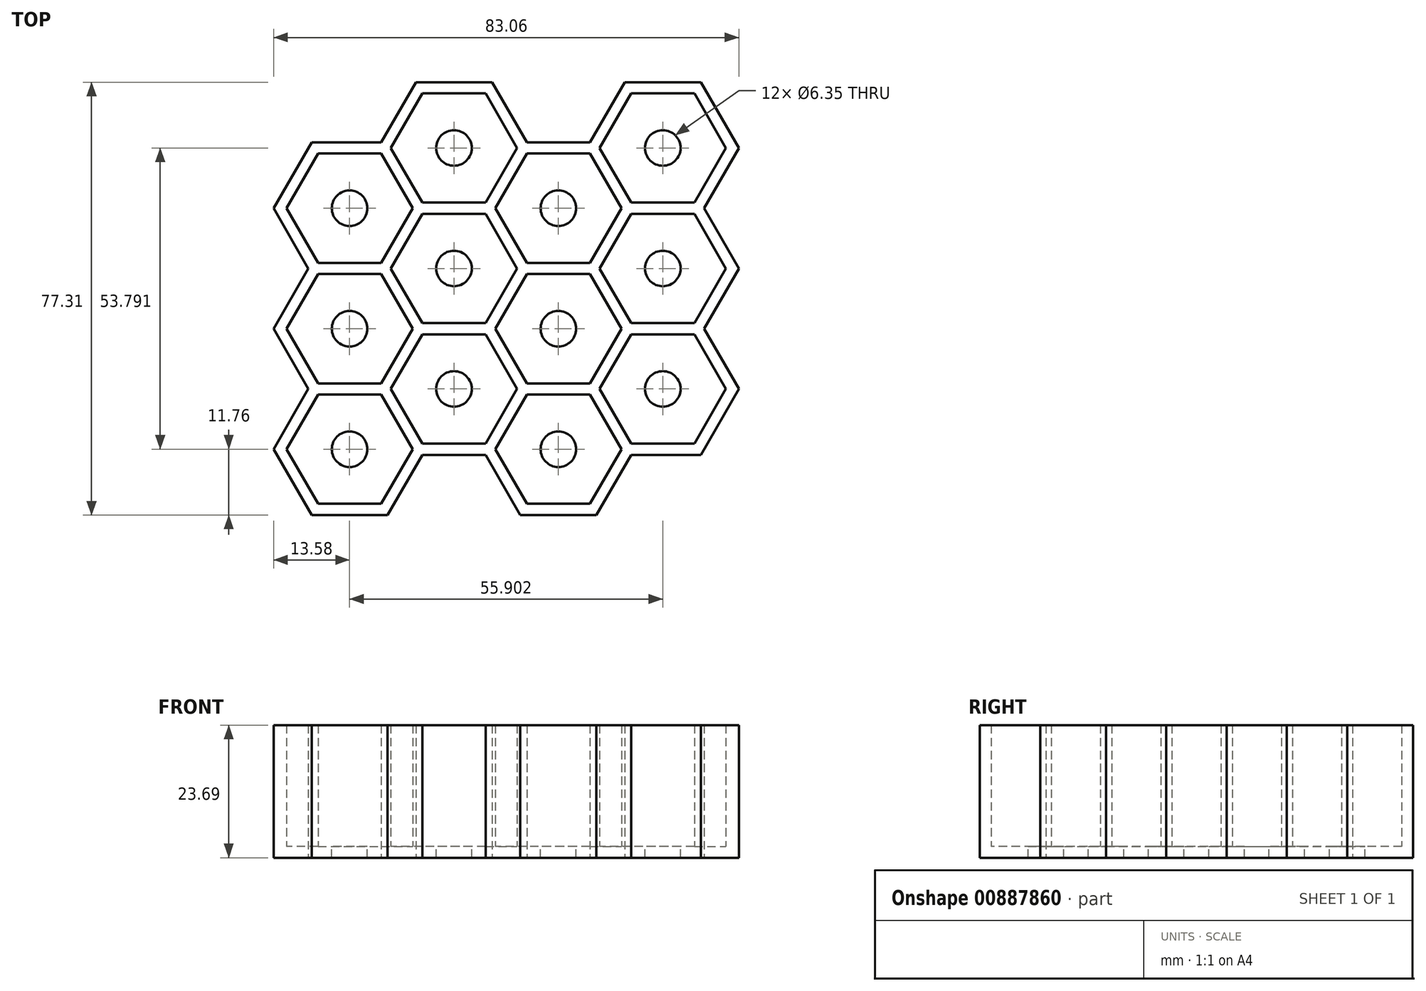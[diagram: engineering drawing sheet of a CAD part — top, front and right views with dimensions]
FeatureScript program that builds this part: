
annotation { "Feature Type Name" : "Feature", "Feature Type Description" : "" }
export const myFeature = defineFeature(function(context is Context, id is Id, definition is map)
    precondition{}
    {
        {
            var Q0;
            Q0=qCreatedBy(makeId("Top.planeOp"),FACE);
            var sketch = newSketch(context, id + "F0", { "sketchPlane" : qUnion([Q0])});
            skCircle(sketch, "E0.cCircle", {"center": v(0, 0) * mm, "radius": 9.76 * mm, "construction": true});
            skLineSegment(sketch, "E0.0", {"start": v(5.63, 9.76) * mm, "end": v(11.27, 0) * mm});
            skLineSegment(sketch, "E0.1", {"start": v(11.27, 0) * mm, "end": v(5.63, -9.76) * mm});
            skLineSegment(sketch, "E0.2", {"start": v(5.63, -9.76) * mm, "end": v(-5.63, -9.76) * mm});
            skLineSegment(sketch, "E0.3", {"start": v(-5.63, -9.76) * mm, "end": v(-11.27, 0) * mm});
            skLineSegment(sketch, "E0.4", {"start": v(-11.27, 0) * mm, "end": v(-5.63, 9.76) * mm});
            skLineSegment(sketch, "E0.5", {"start": v(-5.63, 9.76) * mm, "end": v(5.63, 9.76) * mm});
            skPoint(sketch, "E0.0.midPoint", {"position": v(8.45, 4.88) * mm});
            skPoint(sketch, "E1.0.1.0", {"position": v(8.45, 26.4) * mm});
            skLineSegment(sketch, "E1.0.1.1", {"start": v(5.63, 11.76) * mm, "end": v(-5.63, 11.76) * mm});
            skLineSegment(sketch, "E1.0.1.2", {"start": v(-5.63, 31.27) * mm, "end": v(5.63, 31.27) * mm});
            skCircle(sketch, "E1.0.1.3", {"center": v(0, 21.52) * mm, "radius": 9.76 * mm, "construction": true});
            skLineSegment(sketch, "E1.0.1.4", {"start": v(-5.63, 11.76) * mm, "end": v(-11.27, 21.52) * mm});
            skLineSegment(sketch, "E1.0.1.5", {"start": v(-11.27, 21.52) * mm, "end": v(-5.63, 31.27) * mm});
            skLineSegment(sketch, "E1.0.1.6", {"start": v(5.63, 31.27) * mm, "end": v(11.27, 21.52) * mm});
            skLineSegment(sketch, "E1.0.1.7", {"start": v(11.27, 21.52) * mm, "end": v(5.63, 11.76) * mm});
            skPoint(sketch, "E1.0.2.0", {"position": v(8.45, 47.91) * mm});
            skLineSegment(sketch, "E1.0.2.1", {"start": v(5.63, 33.27) * mm, "end": v(-5.63, 33.27) * mm});
            skLineSegment(sketch, "E1.0.2.2", {"start": v(-5.63, 52.8) * mm, "end": v(5.63, 52.8) * mm});
            skCircle(sketch, "E1.0.2.3", {"center": v(0, 43.03) * mm, "radius": 9.76 * mm, "construction": true});
            skLineSegment(sketch, "E1.0.2.4", {"start": v(-5.63, 33.27) * mm, "end": v(-11.27, 43.03) * mm});
            skLineSegment(sketch, "E1.0.2.5", {"start": v(-11.27, 43.03) * mm, "end": v(-5.63, 52.8) * mm});
            skLineSegment(sketch, "E1.0.2.6", {"start": v(5.63, 52.8) * mm, "end": v(11.27, 43.03) * mm});
            skLineSegment(sketch, "E1.0.2.7", {"start": v(11.27, 43.03) * mm, "end": v(5.63, 33.27) * mm});
            skLineSegment(sketch, "E1.direction1", {"start": v(-5.63, -9.76) * mm, "end": v(27.15, -9.76) * mm, "construction": true});
            skLineSegment(sketch, "E1.direction2", {"start": v(-5.63, -9.76) * mm, "end": v(-5.63, 11.76) * mm, "construction": true});
            skCircle(sketch, "E2.cCircle", {"center": v(18.63, 10.76) * mm, "radius": 9.76 * mm, "construction": true});
            skLineSegment(sketch, "E2.0", {"start": v(24.27, 20.52) * mm, "end": v(29.9, 10.76) * mm});
            skLineSegment(sketch, "E2.1", {"start": v(29.9, 10.76) * mm, "end": v(24.27, 1) * mm});
            skLineSegment(sketch, "E2.2", {"start": v(24.27, 1) * mm, "end": v(13, 1) * mm});
            skLineSegment(sketch, "E2.3", {"start": v(13, 1) * mm, "end": v(7.37, 10.76) * mm});
            skLineSegment(sketch, "E2.4", {"start": v(7.37, 10.76) * mm, "end": v(13, 20.52) * mm});
            skLineSegment(sketch, "E2.5", {"start": v(13, 20.52) * mm, "end": v(24.27, 20.52) * mm});
            skPoint(sketch, "E2.0.midPoint", {"position": v(27.08, 15.64) * mm});
            skLineSegment(sketch, "E3.direction1", {"start": v(13, 1) * mm, "end": v(89.43, 1) * mm, "construction": true});
            skLineSegment(sketch, "E3.direction2", {"start": v(13, 1) * mm, "end": v(13, 51.8) * mm, "construction": true});
            skCircle(sketch, "E4.0.1.0", {"center": v(18.63, 32.27) * mm, "radius": 9.76 * mm, "construction": true});
            skPoint(sketch, "E4.0.1.1", {"position": v(27.08, 37.15) * mm});
            skLineSegment(sketch, "E4.0.1.2", {"start": v(13, 22.52) * mm, "end": v(89.43, 22.52) * mm, "construction": true});
            skLineSegment(sketch, "E4.0.1.3", {"start": v(13, 22.52) * mm, "end": v(7.37, 32.27) * mm});
            skLineSegment(sketch, "E4.0.1.4", {"start": v(13, 22.52) * mm, "end": v(13, 73.32) * mm, "construction": true});
            skLineSegment(sketch, "E4.0.1.5", {"start": v(29.9, 32.27) * mm, "end": v(24.27, 22.52) * mm});
            skLineSegment(sketch, "E4.0.1.6", {"start": v(13, 42.03) * mm, "end": v(24.27, 42.03) * mm});
            skLineSegment(sketch, "E4.0.1.7", {"start": v(7.37, 32.27) * mm, "end": v(13, 42.03) * mm});
            skLineSegment(sketch, "E4.0.1.8", {"start": v(24.27, 22.52) * mm, "end": v(13, 22.52) * mm});
            skLineSegment(sketch, "E4.0.1.9", {"start": v(24.27, 42.03) * mm, "end": v(29.9, 32.27) * mm});
            skCircle(sketch, "E4.0.2.0", {"center": v(18.63, 53.8) * mm, "radius": 9.76 * mm, "construction": true});
            skPoint(sketch, "E4.0.2.1", {"position": v(27.08, 58.67) * mm});
            skLineSegment(sketch, "E4.0.2.2", {"start": v(13, 44.03) * mm, "end": v(89.43, 44.03) * mm, "construction": true});
            skLineSegment(sketch, "E4.0.2.3", {"start": v(13, 44.03) * mm, "end": v(7.37, 53.8) * mm});
            skLineSegment(sketch, "E4.0.2.4", {"start": v(13, 44.03) * mm, "end": v(13, 94.83) * mm, "construction": true});
            skLineSegment(sketch, "E4.0.2.5", {"start": v(29.9, 53.8) * mm, "end": v(24.27, 44.03) * mm});
            skLineSegment(sketch, "E4.0.2.6", {"start": v(13, 63.55) * mm, "end": v(24.27, 63.55) * mm});
            skLineSegment(sketch, "E4.0.2.7", {"start": v(7.37, 53.8) * mm, "end": v(13, 63.55) * mm});
            skLineSegment(sketch, "E4.0.2.8", {"start": v(24.27, 44.03) * mm, "end": v(13, 44.03) * mm});
            skLineSegment(sketch, "E4.0.2.9", {"start": v(24.27, 63.55) * mm, "end": v(29.9, 53.8) * mm});
            skLineSegment(sketch, "E4.direction1", {"start": v(13, 1) * mm, "end": v(50.9, 1) * mm, "construction": true});
            skLineSegment(sketch, "E4.direction2", {"start": v(13, 1) * mm, "end": v(13, 22.52) * mm, "construction": true});
            skLineSegment(sketch, "E5.1.0.0", {"start": v(31.63, -9.76) * mm, "end": v(31.63, 11.76) * mm, "construction": true});
            skLineSegment(sketch, "E5.1.0.1", {"start": v(31.63, 31.27) * mm, "end": v(42.9, 31.27) * mm});
            skLineSegment(sketch, "E5.1.0.3", {"start": v(31.63, 52.8) * mm, "end": v(42.9, 52.8) * mm});
            skPoint(sketch, "E5.1.0.4", {"position": v(45.72, 47.91) * mm});
            skPoint(sketch, "E5.1.0.5", {"position": v(45.72, 26.4) * mm});
            skCircle(sketch, "E5.1.0.6", {"center": v(37.27, 21.52) * mm, "radius": 9.76 * mm, "construction": true});
            skCircle(sketch, "E5.1.0.7", {"center": v(37.27, 0) * mm, "radius": 9.76 * mm, "construction": true});
            skLineSegment(sketch, "E5.1.0.9", {"start": v(42.9, 11.76) * mm, "end": v(31.63, 11.76) * mm});
            skCircle(sketch, "E5.1.0.10", {"center": v(37.27, 43.03) * mm, "radius": 9.76 * mm, "construction": true});
            skPoint(sketch, "E5.1.0.11", {"position": v(45.72, 4.88) * mm});
            skLineSegment(sketch, "E5.1.0.12", {"start": v(42.9, -9.76) * mm, "end": v(31.63, -9.76) * mm});
            skLineSegment(sketch, "E5.1.0.13", {"start": v(42.9, 33.27) * mm, "end": v(31.63, 33.27) * mm});
            skLineSegment(sketch, "E5.1.0.16", {"start": v(48.54, 0) * mm, "end": v(42.9, -9.76) * mm});
            skLineSegment(sketch, "E5.1.0.17", {"start": v(42.9, 9.76) * mm, "end": v(48.54, 0) * mm});
            skLineSegment(sketch, "E5.1.0.20", {"start": v(31.63, 11.76) * mm, "end": v(26, 21.52) * mm});
            skLineSegment(sketch, "E5.1.0.21", {"start": v(42.9, 31.27) * mm, "end": v(48.54, 21.52) * mm});
            skLineSegment(sketch, "E5.1.0.22", {"start": v(48.54, 21.52) * mm, "end": v(42.9, 11.76) * mm});
            skLineSegment(sketch, "E5.1.0.23", {"start": v(26, 0) * mm, "end": v(31.63, 9.76) * mm});
            skLineSegment(sketch, "E5.1.0.24", {"start": v(31.63, 9.76) * mm, "end": v(42.9, 9.76) * mm});
            skLineSegment(sketch, "E5.1.0.25", {"start": v(31.63, -9.76) * mm, "end": v(26, 0) * mm});
            skLineSegment(sketch, "E5.1.0.27", {"start": v(48.54, 43.03) * mm, "end": v(42.9, 33.27) * mm});
            skLineSegment(sketch, "E5.1.0.28", {"start": v(26, 21.52) * mm, "end": v(31.63, 31.27) * mm});
            skLineSegment(sketch, "E5.1.0.29", {"start": v(26, 43.03) * mm, "end": v(31.63, 52.8) * mm});
            skLineSegment(sketch, "E5.1.0.30", {"start": v(42.9, 52.8) * mm, "end": v(48.54, 43.03) * mm});
            skLineSegment(sketch, "E5.1.0.32", {"start": v(31.63, 33.27) * mm, "end": v(26, 43.03) * mm});
            skLineSegment(sketch, "E5.direction1", {"start": v(-5.63, -9.76) * mm, "end": v(31.63, -9.76) * mm, "construction": true});
            skLineSegment(sketch, "E6.0", {"start": v(-13.58, 21.52) * mm, "end": v(-7.37, 32.27) * mm});
            skLineSegment(sketch, "E6.1", {"start": v(-7.37, 10.76) * mm, "end": v(-13.58, 21.52) * mm});
            skLineSegment(sketch, "E7.0", {"start": v(-13.58, 0) * mm, "end": v(-7.37, 10.76) * mm});
            skLineSegment(sketch, "E7.1", {"start": v(-6.79, -11.76) * mm, "end": v(-13.58, 0) * mm});
            skLineSegment(sketch, "E7.2", {"start": v(6.79, -11.76) * mm, "end": v(-6.79, -11.76) * mm});
            skLineSegment(sketch, "E7.3", {"start": v(13, -1) * mm, "end": v(6.79, -11.76) * mm});
            skCircle(sketch, "E8.1.0.1", {"center": v(55.9, 32.27) * mm, "radius": 9.76 * mm, "construction": true});
            skPoint(sketch, "E8.1.0.2", {"position": v(64.35, 58.67) * mm});
            skLineSegment(sketch, "E8.1.0.3", {"start": v(50.27, 44.03) * mm, "end": v(50.27, 94.83) * mm, "construction": true});
            skLineSegment(sketch, "E8.1.0.4", {"start": v(50.27, 1) * mm, "end": v(50.27, 51.8) * mm, "construction": true});
            skLineSegment(sketch, "E8.1.0.5", {"start": v(50.27, 22.52) * mm, "end": v(50.27, 73.32) * mm, "construction": true});
            skPoint(sketch, "E8.1.0.6", {"position": v(64.35, 15.64) * mm});
            skCircle(sketch, "E8.1.0.9", {"center": v(55.9, 10.76) * mm, "radius": 9.76 * mm, "construction": true});
            skPoint(sketch, "E8.1.0.10", {"position": v(64.35, 37.15) * mm});
            skCircle(sketch, "E8.1.0.11", {"center": v(55.9, 53.8) * mm, "radius": 9.76 * mm, "construction": true});
            skLineSegment(sketch, "E8.1.0.14", {"start": v(61.54, 22.52) * mm, "end": v(50.27, 22.52) * mm});
            skLineSegment(sketch, "E8.1.0.15", {"start": v(61.54, 42.03) * mm, "end": v(67.17, 32.27) * mm});
            skLineSegment(sketch, "E8.1.0.16", {"start": v(61.54, 63.55) * mm, "end": v(67.17, 53.8) * mm});
            skLineSegment(sketch, "E8.1.0.17", {"start": v(50.27, 1) * mm, "end": v(44.63, 10.76) * mm});
            skLineSegment(sketch, "E8.1.0.18", {"start": v(61.54, 1) * mm, "end": v(50.27, 1) * mm});
            skLineSegment(sketch, "E8.1.0.21", {"start": v(50.27, 22.52) * mm, "end": v(44.63, 32.27) * mm});
            skLineSegment(sketch, "E8.1.0.22", {"start": v(50.27, 42.03) * mm, "end": v(61.54, 42.03) * mm});
            skLineSegment(sketch, "E8.1.0.23", {"start": v(50.27, 1) * mm, "end": v(50.27, 22.52) * mm, "construction": true});
            skLineSegment(sketch, "E8.1.0.24", {"start": v(61.54, 44.03) * mm, "end": v(50.27, 44.03) * mm});
            skLineSegment(sketch, "E8.1.0.26", {"start": v(44.63, 32.27) * mm, "end": v(50.27, 42.03) * mm});
            skLineSegment(sketch, "E8.1.0.29", {"start": v(67.17, 53.8) * mm, "end": v(61.54, 44.03) * mm});
            skLineSegment(sketch, "E8.1.0.30", {"start": v(50.27, 44.03) * mm, "end": v(44.63, 53.8) * mm});
            skLineSegment(sketch, "E8.1.0.31", {"start": v(44.63, 53.8) * mm, "end": v(50.27, 63.55) * mm});
            skLineSegment(sketch, "E8.1.0.32", {"start": v(50.27, 20.52) * mm, "end": v(61.54, 20.52) * mm});
            skLineSegment(sketch, "E8.1.0.33", {"start": v(44.63, 10.76) * mm, "end": v(50.27, 20.52) * mm});
            skLineSegment(sketch, "E8.1.0.34", {"start": v(67.17, 32.27) * mm, "end": v(61.54, 22.52) * mm});
            skLineSegment(sketch, "E8.1.0.36", {"start": v(50.27, 63.55) * mm, "end": v(61.54, 63.55) * mm});
            skLineSegment(sketch, "E8.1.0.37", {"start": v(67.17, 10.76) * mm, "end": v(61.54, 1) * mm});
            skLineSegment(sketch, "E8.1.0.38", {"start": v(61.54, 20.52) * mm, "end": v(67.17, 10.76) * mm});
            skLineSegment(sketch, "E8.direction1", {"start": v(25.5, -2.85) * mm, "end": v(64.28, -2.85) * mm, "construction": true});
            skLineSegment(sketch, "E9.0", {"start": v(69.48, 32.27) * mm, "end": v(63.27, 21.52) * mm});
            skLineSegment(sketch, "E9.1", {"start": v(63.27, 43.03) * mm, "end": v(69.48, 32.27) * mm});
            skLineSegment(sketch, "E10.0", {"start": v(62.7, -1) * mm, "end": v(50.27, -1) * mm});
            skLineSegment(sketch, "E10.1", {"start": v(69.48, 10.76) * mm, "end": v(62.7, -1) * mm});
            skLineSegment(sketch, "E10.2", {"start": v(63.27, 21.52) * mm, "end": v(69.48, 10.76) * mm});
            skLineSegment(sketch, "E11.0", {"start": v(30.48, -11.76) * mm, "end": v(24.27, -1) * mm});
            skLineSegment(sketch, "E11.1", {"start": v(44.06, -11.76) * mm, "end": v(30.48, -11.76) * mm});
            skLineSegment(sketch, "E11.2", {"start": v(50.27, -1) * mm, "end": v(44.06, -11.76) * mm});
            skLineSegment(sketch, "E12.0", {"start": v(24.27, -1) * mm, "end": v(13, -1) * mm});
            skLineSegment(sketch, "E13.0", {"start": v(-6.79, 54.8) * mm, "end": v(5.63, 54.8) * mm});
            skLineSegment(sketch, "E13.1", {"start": v(-13.58, 43.03) * mm, "end": v(-6.79, 54.8) * mm});
            skLineSegment(sketch, "E13.2", {"start": v(-7.37, 32.27) * mm, "end": v(-13.58, 43.03) * mm});
            skLineSegment(sketch, "E14.0", {"start": v(25.42, 65.55) * mm, "end": v(31.63, 54.8) * mm});
            skLineSegment(sketch, "E14.1", {"start": v(11.85, 65.55) * mm, "end": v(25.42, 65.55) * mm});
            skLineSegment(sketch, "E14.2", {"start": v(5.63, 54.8) * mm, "end": v(11.85, 65.55) * mm});
            skLineSegment(sketch, "E15.0", {"start": v(31.63, 54.8) * mm, "end": v(42.9, 54.8) * mm});
            skLineSegment(sketch, "E16.0", {"start": v(69.48, 53.8) * mm, "end": v(63.27, 43.03) * mm});
            skLineSegment(sketch, "E16.1", {"start": v(62.7, 65.55) * mm, "end": v(69.48, 53.8) * mm});
            skLineSegment(sketch, "E16.2", {"start": v(49.11, 65.55) * mm, "end": v(62.7, 65.55) * mm});
            skLineSegment(sketch, "E16.3", {"start": v(42.9, 54.8) * mm, "end": v(49.11, 65.55) * mm});
            skCircle(sketch, "E17", {"center": v(0, 0) * mm, "radius": 3.18 * mm});
            skCircle(sketch, "E18", {"center": v(0, 21.52) * mm, "radius": 3.18 * mm});
            skCircle(sketch, "E19", {"center": v(0, 43.03) * mm, "radius": 3.18 * mm});
            skCircle(sketch, "E20", {"center": v(18.63, 10.76) * mm, "radius": 3.18 * mm});
            skCircle(sketch, "E21", {"center": v(18.63, 32.27) * mm, "radius": 3.18 * mm});
            skCircle(sketch, "E22", {"center": v(18.63, 53.8) * mm, "radius": 3.18 * mm});
            skCircle(sketch, "E23", {"center": v(37.27, 0) * mm, "radius": 3.18 * mm});
            skCircle(sketch, "E24", {"center": v(37.27, 21.52) * mm, "radius": 3.18 * mm});
            skCircle(sketch, "E25", {"center": v(37.27, 43.03) * mm, "radius": 3.18 * mm});
            skCircle(sketch, "E26", {"center": v(55.9, 53.8) * mm, "radius": 3.18 * mm});
            skCircle(sketch, "E27", {"center": v(55.9, 32.27) * mm, "radius": 3.18 * mm});
            skCircle(sketch, "E28", {"center": v(55.9, 10.76) * mm, "radius": 3.18 * mm});
            skSolve(sketch);
        }
        {
            var Q0;
            Q0=makeQuery(id+"F0.imprint","IMPRINT",FACE,{"disambiguationData":[TD([[makeQuery(id+"F0.imprint","IMPRINT",EDGE,{"derivedFrom":sQuery(id+"F0.wireOp",EDGE,"E0.0")}),1.0]])]});
            extrude(context, id + "F1", {"entities" : qUnion([Q0]), "depth" : 21.7 * mm, "offsetDistance" : 25.4 * mm});
        }
        {
            var Q0;
            Q0=makeQuery(id+"F1.opExtrude","CAP_FACE",FACE,{"disambiguationData":[OSD([sQuery(id+"F0.wireOp",EDGE,"E0.0"),sQuery(id+"F0.wireOp",EDGE,"E0.1"),sQuery(id+"F0.wireOp",EDGE,"E0.2"),sQuery(id+"F0.wireOp",EDGE,"E0.3"),sQuery(id+"F0.wireOp",EDGE,"E0.4"),sQuery(id+"F0.wireOp",EDGE,"E0.5"),sQuery(id+"F0.wireOp",EDGE,"E1.0.1.1"),sQuery(id+"F0.wireOp",EDGE,"E1.0.1.2"),sQuery(id+"F0.wireOp",EDGE,"E1.0.1.4"),sQuery(id+"F0.wireOp",EDGE,"E1.0.1.5"),sQuery(id+"F0.wireOp",EDGE,"E1.0.1.6"),sQuery(id+"F0.wireOp",EDGE,"E1.0.1.7"),sQuery(id+"F0.wireOp",EDGE,"E1.0.2.1"),sQuery(id+"F0.wireOp",EDGE,"E1.0.2.2"),sQuery(id+"F0.wireOp",EDGE,"E1.0.2.4"),sQuery(id+"F0.wireOp",EDGE,"E1.0.2.5"),sQuery(id+"F0.wireOp",EDGE,"E1.0.2.6"),sQuery(id+"F0.wireOp",EDGE,"E1.0.2.7"),sQuery(id+"F0.wireOp",EDGE,"E1.0.3.1"),sQuery(id+"F0.wireOp",EDGE,"E1.0.3.2"),sQuery(id+"F0.wireOp",EDGE,"E1.0.3.4"),sQuery(id+"F0.wireOp",EDGE,"E1.0.3.5"),sQuery(id+"F0.wireOp",EDGE,"E1.0.3.6"),sQuery(id+"F0.wireOp",EDGE,"E1.0.3.7"),sQuery(id+"F0.wireOp",EDGE,"E2.0"),sQuery(id+"F0.wireOp",EDGE,"E2.1"),sQuery(id+"F0.wireOp",EDGE,"E2.2"),sQuery(id+"F0.wireOp",EDGE,"E2.3"),sQuery(id+"F0.wireOp",EDGE,"E2.4"),sQuery(id+"F0.wireOp",EDGE,"E2.5"),sQuery(id+"F0.wireOp",EDGE,"E4.0.1.3"),sQuery(id+"F0.wireOp",EDGE,"E4.0.1.5"),sQuery(id+"F0.wireOp",EDGE,"E4.0.1.6"),sQuery(id+"F0.wireOp",EDGE,"E4.0.1.7"),sQuery(id+"F0.wireOp",EDGE,"E4.0.1.8"),sQuery(id+"F0.wireOp",EDGE,"E4.0.1.9"),sQuery(id+"F0.wireOp",EDGE,"E4.0.2.3"),sQuery(id+"F0.wireOp",EDGE,"E4.0.2.5"),sQuery(id+"F0.wireOp",EDGE,"E4.0.2.6"),sQuery(id+"F0.wireOp",EDGE,"E4.0.2.7"),sQuery(id+"F0.wireOp",EDGE,"E4.0.2.8"),sQuery(id+"F0.wireOp",EDGE,"E4.0.2.9"),sQuery(id+"F0.wireOp",EDGE,"E4.0.3.3"),sQuery(id+"F0.wireOp",EDGE,"E4.0.3.5"),sQuery(id+"F0.wireOp",EDGE,"E4.0.3.6"),sQuery(id+"F0.wireOp",EDGE,"E4.0.3.7"),sQuery(id+"F0.wireOp",EDGE,"E4.0.3.8"),sQuery(id+"F0.wireOp",EDGE,"E4.0.3.9"),sQuery(id+"F0.wireOp",EDGE,"E5.1.0.1"),sQuery(id+"F0.wireOp",EDGE,"E5.1.0.3"),sQuery(id+"F0.wireOp",EDGE,"E5.1.0.9"),sQuery(id+"F0.wireOp",EDGE,"E5.1.0.12"),sQuery(id+"F0.wireOp",EDGE,"E5.1.0.13"),sQuery(id+"F0.wireOp",EDGE,"E5.1.0.14"),sQuery(id+"F0.wireOp",EDGE,"E5.1.0.15"),sQuery(id+"F0.wireOp",EDGE,"E5.1.0.16"),sQuery(id+"F0.wireOp",EDGE,"E5.1.0.17"),sQuery(id+"F0.wireOp",EDGE,"E5.1.0.18"),sQuery(id+"F0.wireOp",EDGE,"E5.1.0.19"),sQuery(id+"F0.wireOp",EDGE,"E5.1.0.20"),sQuery(id+"F0.wireOp",EDGE,"E5.1.0.21"),sQuery(id+"F0.wireOp",EDGE,"E5.1.0.22"),sQuery(id+"F0.wireOp",EDGE,"E5.1.0.23"),sQuery(id+"F0.wireOp",EDGE,"E5.1.0.24"),sQuery(id+"F0.wireOp",EDGE,"E5.1.0.25"),sQuery(id+"F0.wireOp",EDGE,"E5.1.0.26"),sQuery(id+"F0.wireOp",EDGE,"E5.1.0.27"),sQuery(id+"F0.wireOp",EDGE,"E5.1.0.28"),sQuery(id+"F0.wireOp",EDGE,"E5.1.0.29"),sQuery(id+"F0.wireOp",EDGE,"E5.1.0.30"),sQuery(id+"F0.wireOp",EDGE,"E5.1.0.31"),sQuery(id+"F0.wireOp",EDGE,"E5.1.0.32"),sQuery(id+"F0.wireOp",EDGE,"d8c2e539-8584-45db-9c28-70a9466ecaea.0"),sQuery(id+"F0.wireOp",EDGE,"d8c2e539-8584-45db-9c28-70a9466ecaea.1"),sQuery(id+"F0.wireOp",EDGE,"d8c2e539-8584-45db-9c28-70a9466ecaea.2"),sQuery(id+"F0.wireOp",EDGE,"9b3eb7b1-8b51-412c-b289-d74029526f4e.0"),sQuery(id+"F0.wireOp",EDGE,"9b3eb7b1-8b51-412c-b289-d74029526f4e.1"),sQuery(id+"F0.wireOp",EDGE,"9b3eb7b1-8b51-412c-b289-d74029526f4e.2"),sQuery(id+"F0.wireOp",EDGE,"a39cb2d8-247c-408e-99e3-b938a7066d72.0"),sQuery(id+"F0.wireOp",EDGE,"a39cb2d8-247c-408e-99e3-b938a7066d72.1"),sQuery(id+"F0.wireOp",EDGE,"E6.0"),sQuery(id+"F0.wireOp",EDGE,"E6.1"),sQuery(id+"F0.wireOp",EDGE,"E7.0"),sQuery(id+"F0.wireOp",EDGE,"E7.1"),sQuery(id+"F0.wireOp",EDGE,"E7.2"),sQuery(id+"F0.wireOp",EDGE,"E7.3"),sQuery(id+"F0.wireOp",EDGE,"E8.1.0.14"),sQuery(id+"F0.wireOp",EDGE,"E8.1.0.15"),sQuery(id+"F0.wireOp",EDGE,"E8.1.0.16"),sQuery(id+"F0.wireOp",EDGE,"E8.1.0.17"),sQuery(id+"F0.wireOp",EDGE,"E8.1.0.18"),sQuery(id+"F0.wireOp",EDGE,"E8.1.0.19"),sQuery(id+"F0.wireOp",EDGE,"E8.1.0.20"),sQuery(id+"F0.wireOp",EDGE,"E8.1.0.21"),sQuery(id+"F0.wireOp",EDGE,"E8.1.0.22"),sQuery(id+"F0.wireOp",EDGE,"E8.1.0.24"),sQuery(id+"F0.wireOp",EDGE,"E8.1.0.25"),sQuery(id+"F0.wireOp",EDGE,"E8.1.0.26"),sQuery(id+"F0.wireOp",EDGE,"E8.1.0.27"),sQuery(id+"F0.wireOp",EDGE,"E8.1.0.28"),sQuery(id+"F0.wireOp",EDGE,"E8.1.0.29"),sQuery(id+"F0.wireOp",EDGE,"E8.1.0.30"),sQuery(id+"F0.wireOp",EDGE,"E8.1.0.31"),sQuery(id+"F0.wireOp",EDGE,"E8.1.0.32"),sQuery(id+"F0.wireOp",EDGE,"E8.1.0.33"),sQuery(id+"F0.wireOp",EDGE,"E8.1.0.34"),sQuery(id+"F0.wireOp",EDGE,"E8.1.0.35"),sQuery(id+"F0.wireOp",EDGE,"E8.1.0.36"),sQuery(id+"F0.wireOp",EDGE,"E8.1.0.37"),sQuery(id+"F0.wireOp",EDGE,"E8.1.0.38"),sQuery(id+"F0.wireOp",EDGE,"a7611931-1f0c-4c05-9197-59185cbe5667.0"),sQuery(id+"F0.wireOp",EDGE,"04d216cc-bb47-4ca8-a54a-c051a67aae99.0"),sQuery(id+"F0.wireOp",EDGE,"04d216cc-bb47-4ca8-a54a-c051a67aae99.1"),sQuery(id+"F0.wireOp",EDGE,"04d216cc-bb47-4ca8-a54a-c051a67aae99.2"),sQuery(id+"F0.wireOp",EDGE,"04d216cc-bb47-4ca8-a54a-c051a67aae99.3"),sQuery(id+"F0.wireOp",EDGE,"010d73a1-7df7-424b-9d8a-d0a11b36ec60.0"),sQuery(id+"F0.wireOp",EDGE,"010d73a1-7df7-424b-9d8a-d0a11b36ec60.1"),sQuery(id+"F0.wireOp",EDGE,"E9.0"),sQuery(id+"F0.wireOp",EDGE,"E9.1"),sQuery(id+"F0.wireOp",EDGE,"E10.0"),sQuery(id+"F0.wireOp",EDGE,"E10.1"),sQuery(id+"F0.wireOp",EDGE,"E10.2"),sQuery(id+"F0.wireOp",EDGE,"E11.0"),sQuery(id+"F0.wireOp",EDGE,"E11.1"),sQuery(id+"F0.wireOp",EDGE,"E11.2"),sQuery(id+"F0.wireOp",EDGE,"E12.0")])],"isStart":true});
            var sketch = newSketch(context, id + "F2", { "sketchPlane" : qUnion([Q0])});
            skLineSegment(sketch, "E29.0", {"start": v(63.27, -43.03) * mm, "end": v(69.48, -32.27) * mm});
            skLineSegment(sketch, "E30.0", {"start": v(69.48, -32.27) * mm, "end": v(63.27, -21.52) * mm});
            skLineSegment(sketch, "E31.0", {"start": v(63.27, -21.52) * mm, "end": v(69.48, -10.76) * mm});
            skLineSegment(sketch, "E32.0", {"start": v(69.48, -10.76) * mm, "end": v(62.7, 1) * mm});
            skLineSegment(sketch, "E33.0", {"start": v(62.7, 1) * mm, "end": v(50.27, 1) * mm});
            skLineSegment(sketch, "E34.0", {"start": v(50.27, 1) * mm, "end": v(44.06, 11.76) * mm});
            skLineSegment(sketch, "E35.0", {"start": v(44.06, 11.76) * mm, "end": v(30.48, 11.76) * mm});
            skLineSegment(sketch, "E36.0", {"start": v(30.48, 11.76) * mm, "end": v(24.27, 1) * mm});
            skLineSegment(sketch, "E37.0", {"start": v(24.27, 1) * mm, "end": v(13, 1) * mm});
            skLineSegment(sketch, "E38.0", {"start": v(13, 1) * mm, "end": v(6.79, 11.76) * mm});
            skLineSegment(sketch, "E39.0", {"start": v(6.79, 11.76) * mm, "end": v(-6.79, 11.76) * mm});
            skLineSegment(sketch, "E40.0", {"start": v(-6.79, 11.76) * mm, "end": v(-13.58, 0) * mm});
            skLineSegment(sketch, "E41.0", {"start": v(-13.58, 0) * mm, "end": v(-7.37, -10.76) * mm});
            skLineSegment(sketch, "E42.0", {"start": v(-7.37, -10.76) * mm, "end": v(-13.58, -21.52) * mm});
            skLineSegment(sketch, "E43.0", {"start": v(-13.58, -21.52) * mm, "end": v(-13.58, -21.52) * mm});
            skLineSegment(sketch, "E44.0", {"start": v(-13.58, -21.52) * mm, "end": v(-7.37, -32.27) * mm});
            skLineSegment(sketch, "E45.0", {"start": v(69.48, -53.8) * mm, "end": v(63.27, -43.03) * mm});
            skLineSegment(sketch, "E46.0", {"start": v(62.7, -65.55) * mm, "end": v(69.48, -53.8) * mm});
            skLineSegment(sketch, "E47.0", {"start": v(49.11, -65.55) * mm, "end": v(62.7, -65.55) * mm});
            skLineSegment(sketch, "E48.0", {"start": v(42.9, -54.8) * mm, "end": v(49.11, -65.55) * mm});
            skLineSegment(sketch, "E49.0", {"start": v(31.63, -54.8) * mm, "end": v(42.9, -54.8) * mm});
            skLineSegment(sketch, "E50.0", {"start": v(25.42, -65.55) * mm, "end": v(31.63, -54.8) * mm});
            skLineSegment(sketch, "E51.0", {"start": v(11.85, -65.55) * mm, "end": v(25.42, -65.55) * mm});
            skLineSegment(sketch, "E52.0", {"start": v(5.63, -54.8) * mm, "end": v(11.85, -65.55) * mm});
            skLineSegment(sketch, "E53.0", {"start": v(-6.79, -54.8) * mm, "end": v(5.63, -54.8) * mm});
            skLineSegment(sketch, "E54.0", {"start": v(-13.58, -43.03) * mm, "end": v(-6.79, -54.8) * mm});
            skLineSegment(sketch, "E55.0", {"start": v(-7.37, -32.27) * mm, "end": v(-13.58, -43.03) * mm});
            skSolve(sketch);
        }
        {
            var Q0;
            Q0=qSketchRegion(id+"F2",true);
            extrude(context, id + "F3", {"entities" : qUnion([Q0]), "operationType" : NewBodyOperationType.ADD, "depth" : 2 * mm, "offsetDistance" : 25.4 * mm});
        }
        {
            var Q0;
            Q0=makeQuery(id+"F0.imprint","IMPRINT",FACE,{"disambiguationData":[TD([[makeQuery(id+"F0.imprint","IMPRINT",EDGE,{"derivedFrom":sQuery(id+"F0.wireOp",EDGE,"E19")}),1.0]])]});
            var Q1;
            Q1=makeQuery(id+"F0.imprint","IMPRINT",FACE,{"disambiguationData":[TD([[makeQuery(id+"F0.imprint","IMPRINT",EDGE,{"derivedFrom":sQuery(id+"F0.wireOp",EDGE,"E22")}),1.0]])]});
            var Q2;
            Q2=makeQuery(id+"F0.imprint","IMPRINT",FACE,{"disambiguationData":[TD([[makeQuery(id+"F0.imprint","IMPRINT",EDGE,{"derivedFrom":sQuery(id+"F0.wireOp",EDGE,"E25")}),1.0]])]});
            var Q3;
            Q3=makeQuery(id+"F0.imprint","IMPRINT",FACE,{"disambiguationData":[TD([[makeQuery(id+"F0.imprint","IMPRINT",EDGE,{"derivedFrom":sQuery(id+"F0.wireOp",EDGE,"E26")}),1.0]])]});
            var Q4;
            Q4=makeQuery(id+"F0.imprint","IMPRINT",FACE,{"disambiguationData":[TD([[makeQuery(id+"F0.imprint","IMPRINT",EDGE,{"derivedFrom":sQuery(id+"F0.wireOp",EDGE,"E27")}),1.0]])]});
            var Q5;
            Q5=makeQuery(id+"F0.imprint","IMPRINT",FACE,{"disambiguationData":[TD([[makeQuery(id+"F0.imprint","IMPRINT",EDGE,{"derivedFrom":sQuery(id+"F0.wireOp",EDGE,"E24")}),1.0]])]});
            var Q6;
            Q6=makeQuery(id+"F0.imprint","IMPRINT",FACE,{"disambiguationData":[TD([[makeQuery(id+"F0.imprint","IMPRINT",EDGE,{"derivedFrom":sQuery(id+"F0.wireOp",EDGE,"E21")}),1.0]])]});
            var Q7;
            Q7=makeQuery(id+"F0.imprint","IMPRINT",FACE,{"disambiguationData":[TD([[makeQuery(id+"F0.imprint","IMPRINT",EDGE,{"derivedFrom":sQuery(id+"F0.wireOp",EDGE,"E18")}),1.0]])]});
            var Q8;
            Q8=makeQuery(id+"F0.imprint","IMPRINT",FACE,{"disambiguationData":[TD([[makeQuery(id+"F0.imprint","IMPRINT",EDGE,{"derivedFrom":sQuery(id+"F0.wireOp",EDGE,"E17")}),1.0]])]});
            var Q9;
            Q9=makeQuery(id+"F0.imprint","IMPRINT",FACE,{"disambiguationData":[TD([[makeQuery(id+"F0.imprint","IMPRINT",EDGE,{"derivedFrom":sQuery(id+"F0.wireOp",EDGE,"E20")}),1.0]])]});
            var Q10;
            Q10=makeQuery(id+"F0.imprint","IMPRINT",FACE,{"disambiguationData":[TD([[makeQuery(id+"F0.imprint","IMPRINT",EDGE,{"derivedFrom":sQuery(id+"F0.wireOp",EDGE,"E23")}),1.0]])]});
            var Q11;
            Q11=makeQuery(id+"F0.imprint","IMPRINT",FACE,{"disambiguationData":[TD([[makeQuery(id+"F0.imprint","IMPRINT",EDGE,{"derivedFrom":sQuery(id+"F0.wireOp",EDGE,"E28")}),1.0]])]});
            var Q12;
            Q12=makeQuery(id+"F3.opExtrude","CAP_FACE",FACE,{"disambiguationData":[OSD([sQuery(id+"F2.wireOp",EDGE,"E29.0"),sQuery(id+"F2.wireOp",EDGE,"E30.0"),sQuery(id+"F2.wireOp",EDGE,"E31.0"),sQuery(id+"F2.wireOp",EDGE,"E32.0"),sQuery(id+"F2.wireOp",EDGE,"E33.0"),sQuery(id+"F2.wireOp",EDGE,"E34.0"),sQuery(id+"F2.wireOp",EDGE,"E35.0"),sQuery(id+"F2.wireOp",EDGE,"E36.0"),sQuery(id+"F2.wireOp",EDGE,"E37.0"),sQuery(id+"F2.wireOp",EDGE,"E38.0"),sQuery(id+"F2.wireOp",EDGE,"E39.0"),sQuery(id+"F2.wireOp",EDGE,"E40.0"),sQuery(id+"F2.wireOp",EDGE,"E41.0"),sQuery(id+"F2.wireOp",EDGE,"E42.0"),sQuery(id+"F2.wireOp",EDGE,"E44.0"),sQuery(id+"F2.wireOp",EDGE,"E45.0"),sQuery(id+"F2.wireOp",EDGE,"E46.0"),sQuery(id+"F2.wireOp",EDGE,"E47.0"),sQuery(id+"F2.wireOp",EDGE,"E48.0"),sQuery(id+"F2.wireOp",EDGE,"E49.0"),sQuery(id+"F2.wireOp",EDGE,"E50.0"),sQuery(id+"F2.wireOp",EDGE,"E51.0"),sQuery(id+"F2.wireOp",EDGE,"E52.0"),sQuery(id+"F2.wireOp",EDGE,"E53.0"),sQuery(id+"F2.wireOp",EDGE,"E54.0"),sQuery(id+"F2.wireOp",EDGE,"E55.0")])],"isStart":false});
            extrude(context, id + "F4", {"entities" : qUnion([Q0, Q1, Q2, Q3, Q4, Q5, Q6, Q7, Q8, Q9, Q10, Q11]), "operationType" : NewBodyOperationType.REMOVE, "endBound" : BoundingType.UP_TO_SURFACE, "oppositeDirection" : true, "depth" : 25.4 * mm, "endBoundEntityFace" : qUnion([Q12]), "offsetDistance" : 25.4 * mm});
        }
    });
